# Revit family: 306_0b440a72407b4b83abed0bfb61a4a6
name_source: partatom
category: Pipe Accessories
units: mm (PartAtom-declared; Revit-internal decimal feet)

## family parameters
Always vertical = Yes
Cut with Voids When Loaded = No
Part Type = Valve - Breaks Into
Round Connector Dimension = Use Diameter
Shared = No
Work Plane-Based = No

## types (2) — shared parameters
A1 = 2 mm  [stored 0.00656168 ft]
A2 = 25 mm  [stored 0.082021 ft]
A3 = 24 mm  [stored 0.0787402 ft]
A4 = 19 mm
A5 = 17 mm  [stored 0.0557743 ft]
B = 62 mm  [stored 0.203412 ft]
C = 60 mm  [stored 0.19685 ft]
CT2 = 24 mm  [stored 0.0787402 ft]
Description = Thermostatic mixing valve VTA572, PN10 external thread
L2D = 68 mm
L2D_Min = 3048 mm  [stored 10 ft]
LT2 = 34 mm  [stored 0.111549 ft]
MC = No
Manufacturer = ESBE
QmdConnectorList = 301;D;302;D
URL = http://www.esbe.eu
W1 = 21 mm  [stored 0.0688976 ft]
W2 = 19 mm
WT2 = 28 mm  [stored 0.0918635 ft]
X1 = 2 mm  [stored 0.00656168 ft]
X2 = 8 mm  [stored 0.0262467 ft]
X3 = 64 mm  [stored 0.209974 ft]
X4 = 56 mm  [stored 0.183727 ft]
X7 = 4 mm  [stored 0.0131234 ft]
X7__ve = -4 mm  [stored -0.0131234 ft]
Z1 = 7 mm  [stored 0.0229659 ft]
Z1__ve = -7 mm
Z3 = 5 mm  [stored 0.0164042 ft]
Z4 = 16 mm  [stored 0.0524934 ft]
magiPartTypeId = 306
magiProductFamilyId = 0b440a72407b4b83abed0bfb61a4a6

## per-type parameters (varying)
| type | A | A__ve | D | DT2 | R2 | W2D | Z2 | magiProductId |
| VTA572 20-55°C G1 1/4 -4,8 | 38 mm | -38 mm  [stored -0.124672 ft] | 32 mm | 16 mm  [stored 0.0524934 ft] | 14 mm  [stored 0.0459318 ft] | 32 mm  [stored 0.104987 ft] | 27 mm | aadb661fddc44bf18c91cf0c0ba0d4 |
| VTA572 20-55°C G1-4,5 | 35 mm | -35 mm | 25 mm | 13 mm | 11 mm | 25 mm  [stored 0.082021 ft] | 29 mm | ff91f019156343b1a5ba01001ec90a |

note: column(s) folded — value = type name in every type: magiProductCode

note: [stored X ft] marks values corroborated as IEEE doubles in the binary element streams (Revit-internal decimal feet)

## geometry (parser evidence)
native form markers: Sweep x1
no freeform markers — native parametric forms only
